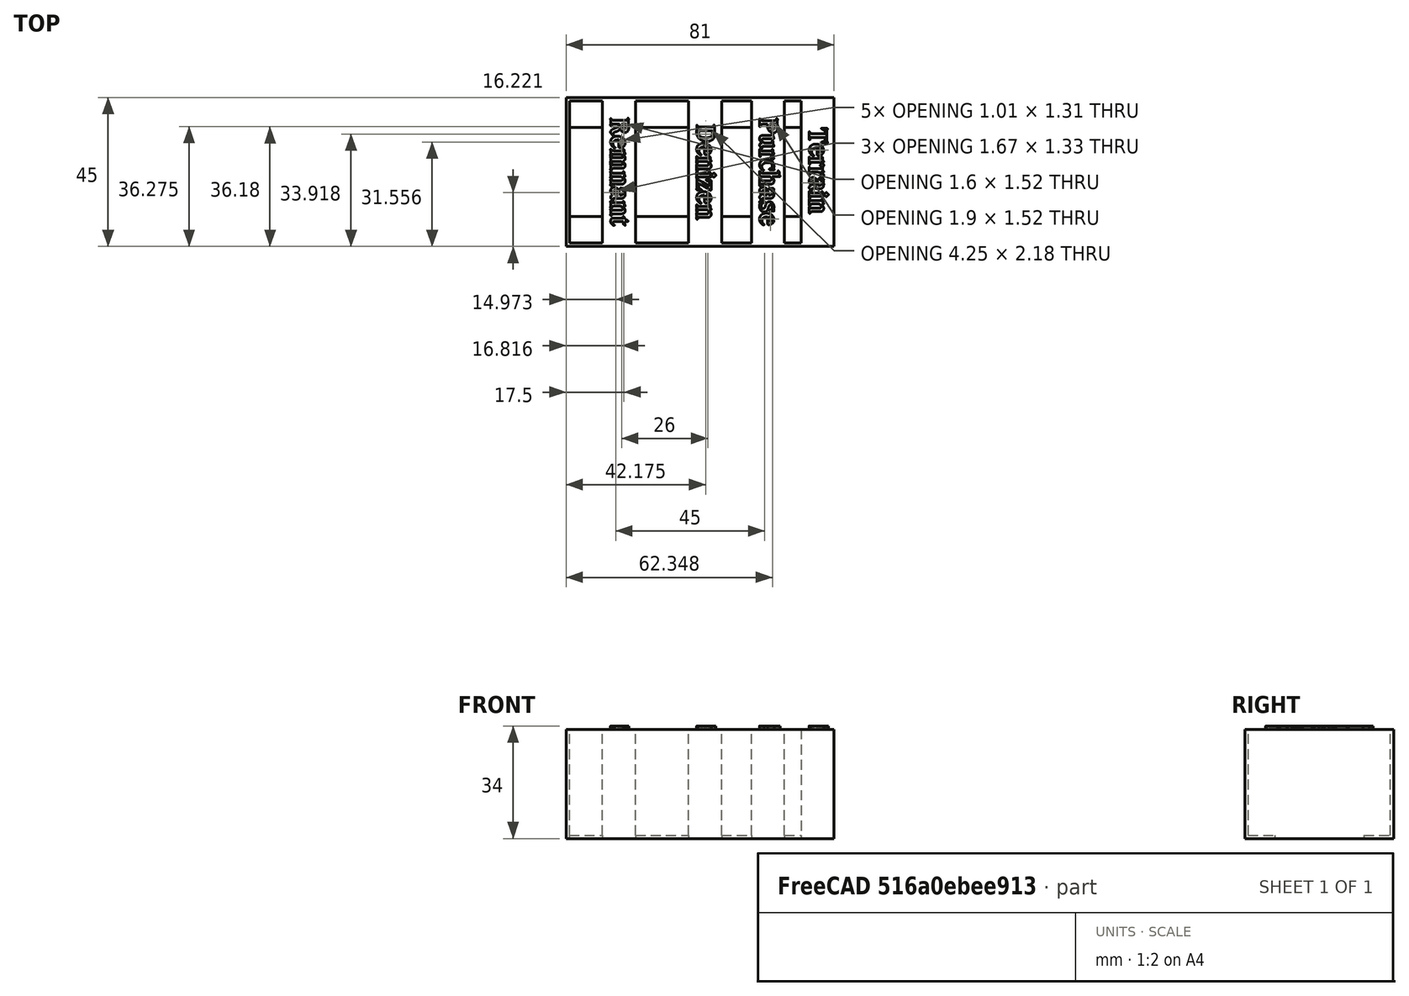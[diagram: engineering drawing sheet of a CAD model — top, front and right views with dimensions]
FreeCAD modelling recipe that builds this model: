
FCSTD DOCUMENT  (FreeCAD 0.18R4 (GitTag))
Label: cataclysm
License: All rights reserved
LicenseURL: http://en.wikipedia.org/wiki/All_rights_reserved
objects: Part::Box×9, Part::Extrusion×8, Part::MultiFuse×7, Part::Part2DObjectPython×4, Part::Cut×2
note: 30 computed .brp shape members not serialized (recipe doc carries the construction recipe); baked Part::Feature solids carry a one-line shape summary decoded from their .brp

FEATURE [Part::Box] Box  label="Cube"
  AttacherType = Attacher::AttachEngine3D
  Height = 33
  Length = 202
  Placement = pos=(0,-1,0) rot=(0,0,1;0rad)
  Width = 45
FEATURE [Part::Box] Box001  label="Cube001"
  AttacherType = Attacher::AttachEngine3D
  Height = 33
  Length = 200
  Placement = pos=(1,0,0) rot=(0,0,1;0rad)
  Width = 43
FEATURE [Part::Cut] Cut
  Base = -> Box
  Tool = -> Box001
FEATURE [Part::Box] Box002  label="Cube002"
  AttacherType = Attacher::AttachEngine3D
  Height = 1
  Length = 202
  Width = 8
FEATURE [Part::Box] Box003  label="Cube003"
  AttacherType = Attacher::AttachEngine3D
  Height = 1
  Length = 202
  Placement = pos=(0,35,0) rot=(0,0,1;0rad)
  Width = 8
FEATURE [Part::MultiFuse] Fusion
  Shapes = -> [Cut,Box002,Box003]
FEATURE [Part::Box] Box004  label="Cube004"
  AttacherType = Attacher::AttachEngine3D
  Height = 33
  Length = 10
  Placement = pos=(11,0,0) rot=(0,0,1;0rad)
  Width = 43
FEATURE [Part::Box] Box005  label="Cube005"
  AttacherType = Attacher::AttachEngine3D
  Height = 33
  Length = 10
  Placement = pos=(37,0,0) rot=(0,0,1;0rad)
  Width = 43
FEATURE [Part::Box] Box006  label="Cube006"
  AttacherType = Attacher::AttachEngine3D
  Height = 33
  Length = 10
  Placement = pos=(56,0,0) rot=(0,0,1;0rad)
  Width = 43
FEATURE [Part::Box] Box007  label="Cube007"
  AttacherType = Attacher::AttachEngine3D
  Height = 33
  Length = 10
  Placement = pos=(71,-1,0) rot=(0,0,1;0rad)
  Width = 45
FEATURE [Part::Box] Box008  label="Cube008"
  AttacherType = Attacher::AttachEngine3D
  Height = 35
  Length = 121
  Placement = pos=(81,-1,0) rot=(0,0,1;0rad)
  Width = 45
FEATURE [Part::MultiFuse] Fusion001
  Shapes = -> [Fusion,Box004,Box005,Box006,Box007]
FEATURE [Part::Cut] Cut001
  Base = -> Fusion001
  Tool = -> Box008
FEATURE [Part::Part2DObjectPython] ShapeString  # Draft 2D object (typed FeaturePython)
  FontFile = <userpath>/Downloads/talisman/Caxton Bold.otf
  Placement = pos=(90.59,34.86,33) rot=(0,0,-1;1.5708rad)
  Size = 3
  String = Terrain
  Tracking = 0
FEATURE [Part::Part2DObjectPython] ShapeString001  # Draft 2D object (typed FeaturePython)
  FontFile = <userpath>/Downloads/talisman/Caxton Bold.otf
  Placement = pos=(90.59,34.86,33) rot=(0,0,-1;1.5708rad)
  Size = 3
  String = Denizen
  Tracking = 0
FEATURE [Part::Part2DObjectPython] ShapeString002  # Draft 2D object (typed FeaturePython)
  FontFile = <userpath>/Downloads/talisman/Caxton Bold.otf
  Placement = pos=(90.59,34.86,33) rot=(0,0,-1;1.5708rad)
  Size = 3
  String = Remnant
  Tracking = 0
FEATURE [Part::Part2DObjectPython] ShapeString003  # Draft 2D object (typed FeaturePython)
  FontFile = <userpath>/Downloads/talisman/Caxton Bold.otf
  Placement = pos=(90.59,34.86,33) rot=(0,0,-1;1.5708rad)
  Size = 3
  String = Purchase
  Tracking = 0
FEATURE [Part::Extrusion] Extrude
  Base = -> ShapeString
  Dir = (0,0,1)
  DirMode = 2
  FaceMakerClass = Part::FaceMakerBullseye
  LengthFwd = 1
  LengthRev = 0
  Solid = false
  Symmetric = false
FEATURE [Part::Extrusion] Extrude001
  Base = -> ShapeString001
  Dir = (0,0,1)
  DirMode = 2
  FaceMakerClass = Part::FaceMakerBullseye
  LengthFwd = 1
  LengthRev = 0
  Solid = false
  Symmetric = false
FEATURE [Part::Extrusion] Extrude002
  Base = -> ShapeString002
  Dir = (0,0,1)
  DirMode = 2
  FaceMakerClass = Part::FaceMakerBullseye
  LengthFwd = 1
  LengthRev = 0
  Solid = false
  Symmetric = false
FEATURE [Part::Extrusion] Extrude003
  Base = -> ShapeString003
  Dir = (0,0,1)
  DirMode = 2
  FaceMakerClass = Part::FaceMakerBullseye
  LengthFwd = 1
  LengthRev = 0
  Solid = false
  Symmetric = false
FEATURE [Part::Extrusion] Extrude004
  Base = -> ShapeString
  Dir = (0,0,1)
  DirMode = 2
  FaceMakerClass = Part::FaceMakerBullseye
  LengthFwd = 1
  LengthRev = 0
  Solid = false
  Symmetric = false
FEATURE [Part::Extrusion] Extrude005
  Base = -> ShapeString001
  Dir = (0,0,1)
  DirMode = 2
  FaceMakerClass = Part::FaceMakerBullseye
  LengthFwd = 1
  LengthRev = 0
  Solid = false
  Symmetric = false
FEATURE [Part::Extrusion] Extrude006
  Base = -> ShapeString002
  Dir = (0,0,1)
  DirMode = 2
  FaceMakerClass = Part::FaceMakerBullseye
  LengthFwd = 1
  LengthRev = 0
  Solid = false
  Symmetric = false
FEATURE [Part::Extrusion] Extrude007
  Base = -> ShapeString003
  Dir = (0,0,1)
  DirMode = 2
  FaceMakerClass = Part::FaceMakerBullseye
  LengthFwd = 1
  LengthRev = 0
  Solid = false
  Symmetric = false
FEATURE [Part::MultiFuse] Fusion002
  Placement = pos=(-17,0,0) rot=(0,0,1;0rad)
  Shapes = -> [Extrude,Extrude004]
FEATURE [Part::MultiFuse] Fusion003
  Placement = pos=(-51,1,0) rot=(0,0,1;0rad)
  Shapes = -> [Extrude001,Extrude005]
FEATURE [Part::MultiFuse] Fusion004
  Placement = pos=(-77,3,0) rot=(0,0,1;0rad)
  Shapes = -> [Extrude002,Extrude006]
FEATURE [Part::MultiFuse] Fusion005
  Placement = pos=(-32,3,0) rot=(0,0,1;0rad)
  Shapes = -> [Extrude003,Extrude007]
FEATURE [Part::MultiFuse] Fusion006
  Shapes = -> [Fusion004,Fusion005,Fusion003,Fusion002]
